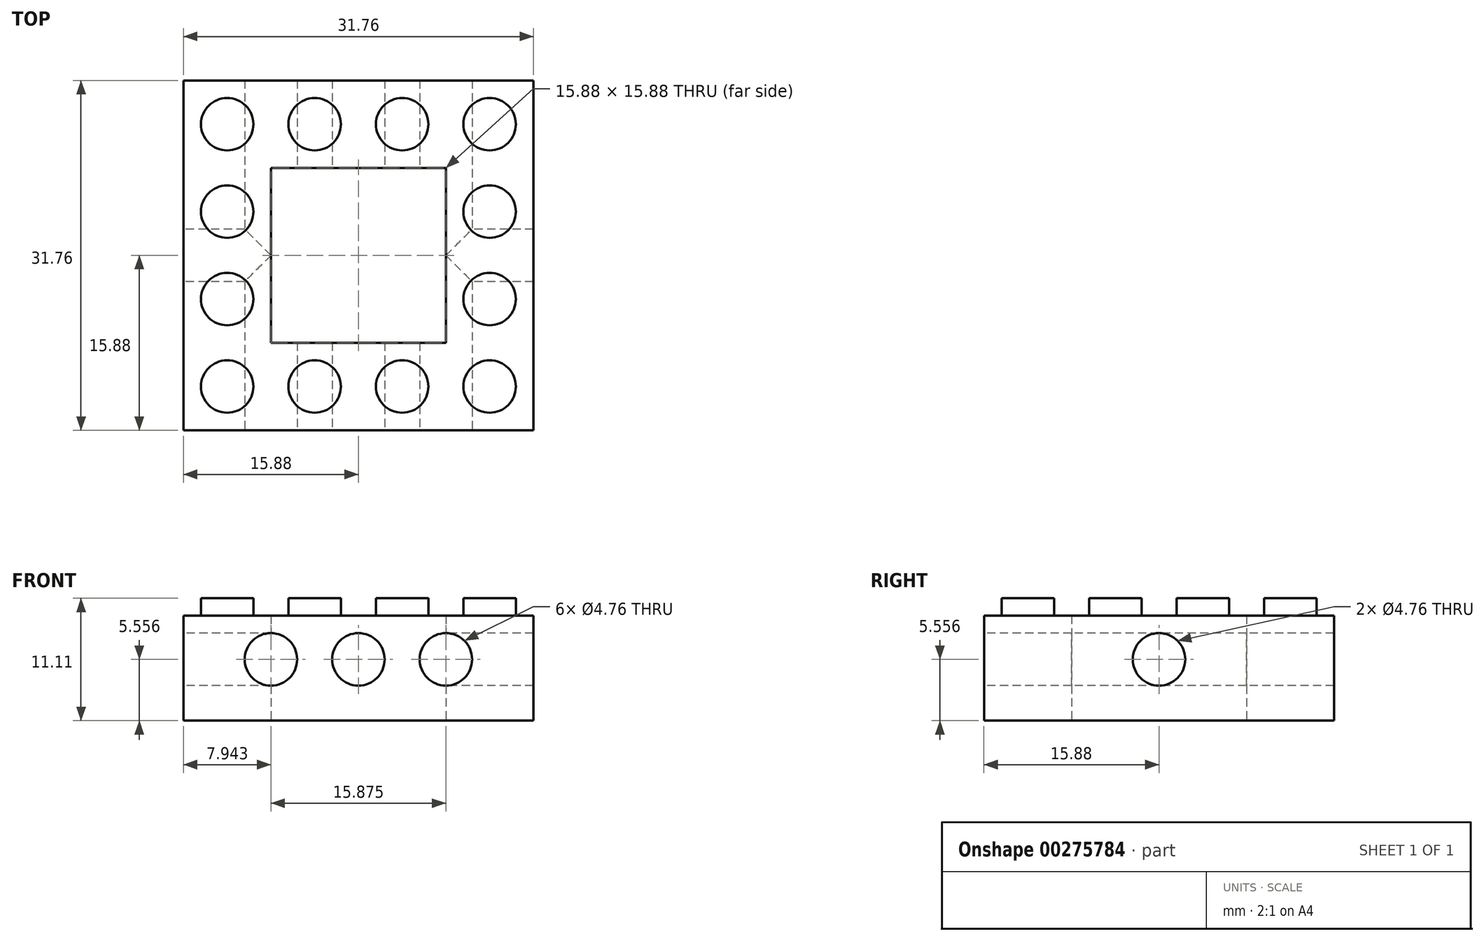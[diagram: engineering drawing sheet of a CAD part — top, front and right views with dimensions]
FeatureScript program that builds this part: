
annotation { "Feature Type Name" : "Feature", "Feature Type Description" : "" }
export const myFeature = defineFeature(function(context is Context, id is Id, definition is map)
    precondition{}
    {
        {
            var Q0;
            Q0=qCreatedBy(makeId("Top.planeOp"),FACE);
            var sketch = newSketch(context, id + "F0", { "sketchPlane" : qUnion([Q0])});
            skLineSegment(sketch, "E0.bottom", {"start": v(-15.88, 15.88) * mm, "end": v(15.88, 15.88) * mm});
            skLineSegment(sketch, "E0.top", {"start": v(-15.88, -15.88) * mm, "end": v(15.88, -15.88) * mm});
            skLineSegment(sketch, "E0.left", {"start": v(-15.87, 15.88) * mm, "end": v(-15.88, -15.88) * mm});
            skLineSegment(sketch, "E0.right", {"start": v(15.88, 15.88) * mm, "end": v(15.88, -15.88) * mm});
            skPoint(sketch, "E0.middle", {"position": v(0, 0) * mm});
            skCircle(sketch, "E1", {"center": v(-11.9, -11.9) * mm, "radius": 2.38 * mm});
            skCircle(sketch, "E2.0.1.0", {"center": v(-11.9, -3.97) * mm, "radius": 2.38 * mm});
            skCircle(sketch, "E2.0.2.0", {"center": v(-11.9, 3.97) * mm, "radius": 2.38 * mm});
            skCircle(sketch, "E2.0.3.0", {"center": v(-11.9, 11.9) * mm, "radius": 2.38 * mm});
            skCircle(sketch, "E2.1.0.0", {"center": v(-3.97, -11.9) * mm, "radius": 2.38 * mm});
            skCircle(sketch, "E2.1.1.0", {"center": v(-3.97, -3.97) * mm, "radius": 2.38 * mm});
            skCircle(sketch, "E2.1.2.0", {"center": v(-3.97, 3.97) * mm, "radius": 2.38 * mm});
            skCircle(sketch, "E2.1.3.0", {"center": v(-3.97, 11.9) * mm, "radius": 2.38 * mm});
            skCircle(sketch, "E2.2.0.0", {"center": v(3.97, -11.9) * mm, "radius": 2.38 * mm});
            skCircle(sketch, "E2.2.1.0", {"center": v(3.97, -3.97) * mm, "radius": 2.38 * mm});
            skCircle(sketch, "E2.2.2.0", {"center": v(3.97, 3.97) * mm, "radius": 2.38 * mm});
            skCircle(sketch, "E2.2.3.0", {"center": v(3.97, 11.9) * mm, "radius": 2.38 * mm});
            skCircle(sketch, "E2.3.0.0", {"center": v(11.9, -11.9) * mm, "radius": 2.38 * mm});
            skCircle(sketch, "E2.3.1.0", {"center": v(11.9, -3.97) * mm, "radius": 2.38 * mm});
            skCircle(sketch, "E2.3.2.0", {"center": v(11.9, 3.97) * mm, "radius": 2.38 * mm});
            skCircle(sketch, "E2.3.3.0", {"center": v(11.9, 11.9) * mm, "radius": 2.38 * mm});
            skLineSegment(sketch, "E2.direction1", {"start": v(-11.9, -11.9) * mm, "end": v(-3.97, -11.9) * mm, "construction": true});
            skLineSegment(sketch, "E2.direction2", {"start": v(-11.9, -11.9) * mm, "end": v(-11.9, -3.97) * mm, "construction": true});
            skSolve(sketch);
        }
        {
            var Q0;
            Q0=qSketchRegion(id+"F0",true);
            extrude(context, id + "F1", {"entities" : qUnion([Q0]), "depth" : 9.52 * mm});
        }
        {
            var Q0;
            Q0=makeQuery(id+"F0.imprint","IMPRINT",FACE,{"disambiguationData":[TD([[makeQuery(id+"F0.imprint","IMPRINT",EDGE,{"derivedFrom":sQuery(id+"F0.wireOp",EDGE,"E2.0.3.0")}),1.0]])]});
            var Q1;
            Q1=makeQuery(id+"F0.imprint","IMPRINT",FACE,{"disambiguationData":[TD([[makeQuery(id+"F0.imprint","IMPRINT",EDGE,{"derivedFrom":sQuery(id+"F0.wireOp",EDGE,"E2.1.3.0")}),1.0]])]});
            var Q2;
            Q2=makeQuery(id+"F0.imprint","IMPRINT",FACE,{"disambiguationData":[TD([[makeQuery(id+"F0.imprint","IMPRINT",EDGE,{"derivedFrom":sQuery(id+"F0.wireOp",EDGE,"E2.2.3.0")}),1.0]])]});
            var Q3;
            Q3=makeQuery(id+"F0.imprint","IMPRINT",FACE,{"disambiguationData":[TD([[makeQuery(id+"F0.imprint","IMPRINT",EDGE,{"derivedFrom":sQuery(id+"F0.wireOp",EDGE,"E2.3.3.0")}),1.0]])]});
            var Q4;
            Q4=makeQuery(id+"F0.imprint","IMPRINT",FACE,{"disambiguationData":[TD([[makeQuery(id+"F0.imprint","IMPRINT",EDGE,{"derivedFrom":sQuery(id+"F0.wireOp",EDGE,"E2.3.2.0")}),1.0]])]});
            var Q5;
            Q5=makeQuery(id+"F0.imprint","IMPRINT",FACE,{"disambiguationData":[TD([[makeQuery(id+"F0.imprint","IMPRINT",EDGE,{"derivedFrom":sQuery(id+"F0.wireOp",EDGE,"E2.2.2.0")}),1.0]])]});
            var Q6;
            Q6=makeQuery(id+"F0.imprint","IMPRINT",FACE,{"disambiguationData":[TD([[makeQuery(id+"F0.imprint","IMPRINT",EDGE,{"derivedFrom":sQuery(id+"F0.wireOp",EDGE,"E2.1.2.0")}),1.0]])]});
            var Q7;
            Q7=makeQuery(id+"F0.imprint","IMPRINT",FACE,{"disambiguationData":[TD([[makeQuery(id+"F0.imprint","IMPRINT",EDGE,{"derivedFrom":sQuery(id+"F0.wireOp",EDGE,"E2.0.2.0")}),1.0]])]});
            var Q8;
            Q8=makeQuery(id+"F0.imprint","IMPRINT",FACE,{"disambiguationData":[TD([[makeQuery(id+"F0.imprint","IMPRINT",EDGE,{"derivedFrom":sQuery(id+"F0.wireOp",EDGE,"E2.0.1.0")}),1.0]])]});
            var Q9;
            Q9=makeQuery(id+"F0.imprint","IMPRINT",FACE,{"disambiguationData":[TD([[makeQuery(id+"F0.imprint","IMPRINT",EDGE,{"derivedFrom":sQuery(id+"F0.wireOp",EDGE,"E2.1.1.0")}),1.0]])]});
            var Q10;
            Q10=makeQuery(id+"F0.imprint","IMPRINT",FACE,{"disambiguationData":[TD([[makeQuery(id+"F0.imprint","IMPRINT",EDGE,{"derivedFrom":sQuery(id+"F0.wireOp",EDGE,"E2.2.1.0")}),1.0]])]});
            var Q11;
            Q11=makeQuery(id+"F0.imprint","IMPRINT",FACE,{"disambiguationData":[TD([[makeQuery(id+"F0.imprint","IMPRINT",EDGE,{"derivedFrom":sQuery(id+"F0.wireOp",EDGE,"E2.3.1.0")}),1.0]])]});
            var Q12;
            Q12=makeQuery(id+"F0.imprint","IMPRINT",FACE,{"disambiguationData":[TD([[makeQuery(id+"F0.imprint","IMPRINT",EDGE,{"derivedFrom":sQuery(id+"F0.wireOp",EDGE,"E2.3.0.0")}),1.0]])]});
            var Q13;
            Q13=makeQuery(id+"F0.imprint","IMPRINT",FACE,{"disambiguationData":[TD([[makeQuery(id+"F0.imprint","IMPRINT",EDGE,{"derivedFrom":sQuery(id+"F0.wireOp",EDGE,"E2.2.0.0")}),1.0]])]});
            var Q14;
            Q14=makeQuery(id+"F0.imprint","IMPRINT",FACE,{"disambiguationData":[TD([[makeQuery(id+"F0.imprint","IMPRINT",EDGE,{"derivedFrom":sQuery(id+"F0.wireOp",EDGE,"E2.1.0.0")}),1.0]])]});
            var Q15;
            Q15=makeQuery(id+"F0.imprint","IMPRINT",FACE,{"disambiguationData":[TD([[makeQuery(id+"F0.imprint","IMPRINT",EDGE,{"derivedFrom":sQuery(id+"F0.wireOp",EDGE,"E1")}),1.0]])]});
            extrude(context, id + "F2", {"entities" : qUnion([Q0, Q1, Q2, Q3, Q4, Q5, Q6, Q7, Q8, Q9, Q10, Q11, Q12, Q13, Q14, Q15]), "operationType" : NewBodyOperationType.ADD, "depth" : 11.1 * mm});
        }
        {
            var Q0;
            Q0=makeQuery(id+"F1.opExtrude","CAP_FACE",FACE,{"disambiguationData":[OSD([sQuery(id+"F0.wireOp",EDGE,"E0.bottom"),sQuery(id+"F0.wireOp",EDGE,"E0.top"),sQuery(id+"F0.wireOp",EDGE,"E0.left"),sQuery(id+"F0.wireOp",EDGE,"E0.right"),sQuery(id+"F0.wireOp",EDGE,"E1"),sQuery(id+"F0.wireOp",EDGE,"E2.0.1.0"),sQuery(id+"F0.wireOp",EDGE,"E2.0.2.0"),sQuery(id+"F0.wireOp",EDGE,"E2.0.3.0"),sQuery(id+"F0.wireOp",EDGE,"E2.1.0.0"),sQuery(id+"F0.wireOp",EDGE,"E2.1.1.0"),sQuery(id+"F0.wireOp",EDGE,"E2.1.2.0"),sQuery(id+"F0.wireOp",EDGE,"E2.1.3.0"),sQuery(id+"F0.wireOp",EDGE,"E2.2.0.0"),sQuery(id+"F0.wireOp",EDGE,"E2.2.1.0"),sQuery(id+"F0.wireOp",EDGE,"E2.2.2.0"),sQuery(id+"F0.wireOp",EDGE,"E2.2.3.0"),sQuery(id+"F0.wireOp",EDGE,"E2.3.0.0"),sQuery(id+"F0.wireOp",EDGE,"E2.3.1.0"),sQuery(id+"F0.wireOp",EDGE,"E2.3.2.0"),sQuery(id+"F0.wireOp",EDGE,"E2.3.3.0")])],"isStart":false});
            var sketch = newSketch(context, id + "F3", { "sketchPlane" : qUnion([Q0])});
            skLineSegment(sketch, "E3.bottom", {"start": v(-7.94, 7.94) * mm, "end": v(7.94, 7.94) * mm});
            skLineSegment(sketch, "E3.top", {"start": v(-7.94, -7.94) * mm, "end": v(7.94, -7.94) * mm});
            skLineSegment(sketch, "E3.left", {"start": v(-7.94, 7.94) * mm, "end": v(-7.94, -7.94) * mm});
            skLineSegment(sketch, "E3.right", {"start": v(7.94, 7.94) * mm, "end": v(7.94, -7.94) * mm});
            skPoint(sketch, "E3.middle", {"position": v(0, 0) * mm});
            skSolve(sketch);
        }
        {
            var Q0;
            Q0=qSketchRegion(id+"F3",true);
            extrude(context, id + "F4", {"entities" : qUnion([Q0]), "operationType" : NewBodyOperationType.REMOVE, "endBound" : BoundingType.SYMMETRIC, "depth" : 25.4 * mm});
        }
        {
            var Q0;
            Q0=makeQuery(id+"F1.opExtrude","SWEPT_FACE",FACE,{"disambiguationData":[OSD([sQuery(id+"F0.wireOp",EDGE,"E0.top")])]});
            var sketch = newSketch(context, id + "F5", { "sketchPlane" : qUnion([Q0])});
            skCircle(sketch, "E4", {"center": v(0, 5.56) * mm, "radius": 2.38 * mm});
            skCircle(sketch, "E5", {"center": v(-7.94, 5.56) * mm, "radius": 2.38 * mm});
            skCircle(sketch, "E6", {"center": v(7.94, 5.56) * mm, "radius": 2.38 * mm});
            skSolve(sketch);
        }
        {
            var Q0;
            Q0=makeQuery(id+"F5.imprint","IMPRINT",FACE,{"disambiguationData":[TD([[makeQuery(id+"F5.imprint","IMPRINT",EDGE,{"derivedFrom":sQuery(id+"F5.wireOp",EDGE,"E6")}),1.0]])]});
            var Q1;
            Q1=makeQuery(id+"F5.imprint","IMPRINT",FACE,{"disambiguationData":[TD([[makeQuery(id+"F5.imprint","IMPRINT",EDGE,{"derivedFrom":sQuery(id+"F5.wireOp",EDGE,"E4")}),1.0]])]});
            var Q2;
            Q2=makeQuery(id+"F5.imprint","IMPRINT",FACE,{"disambiguationData":[TD([[makeQuery(id+"F5.imprint","IMPRINT",EDGE,{"derivedFrom":sQuery(id+"F5.wireOp",EDGE,"E5")}),1.0]])]});
            extrude(context, id + "F6", {"entities" : qUnion([Q0, Q1, Q2]), "operationType" : NewBodyOperationType.REMOVE, "oppositeDirection" : true, "depth" : 50.8 * mm});
        }
        {
            var Q0;
            Q0=makeQuery(id+"F1.opExtrude","SWEPT_FACE",FACE,{"disambiguationData":[OSD([sQuery(id+"F0.wireOp",EDGE,"E0.left")])]});
            var sketch = newSketch(context, id + "F7", { "sketchPlane" : qUnion([Q0])});
            skLineSegment(sketch, "E7", {"start": v(0, 0) * mm, "end": v(0, 5.56) * mm});
            skCircle(sketch, "E8", {"center": v(0, 5.56) * mm, "radius": 2.38 * mm});
            skSolve(sketch);
        }
        {
            var Q0;
            Q0=qSketchRegion(id+"F7",true);
            extrude(context, id + "F8", {"entities" : qUnion([Q0]), "operationType" : NewBodyOperationType.REMOVE, "oppositeDirection" : true, "depth" : 50.8 * mm});
        }
    });
